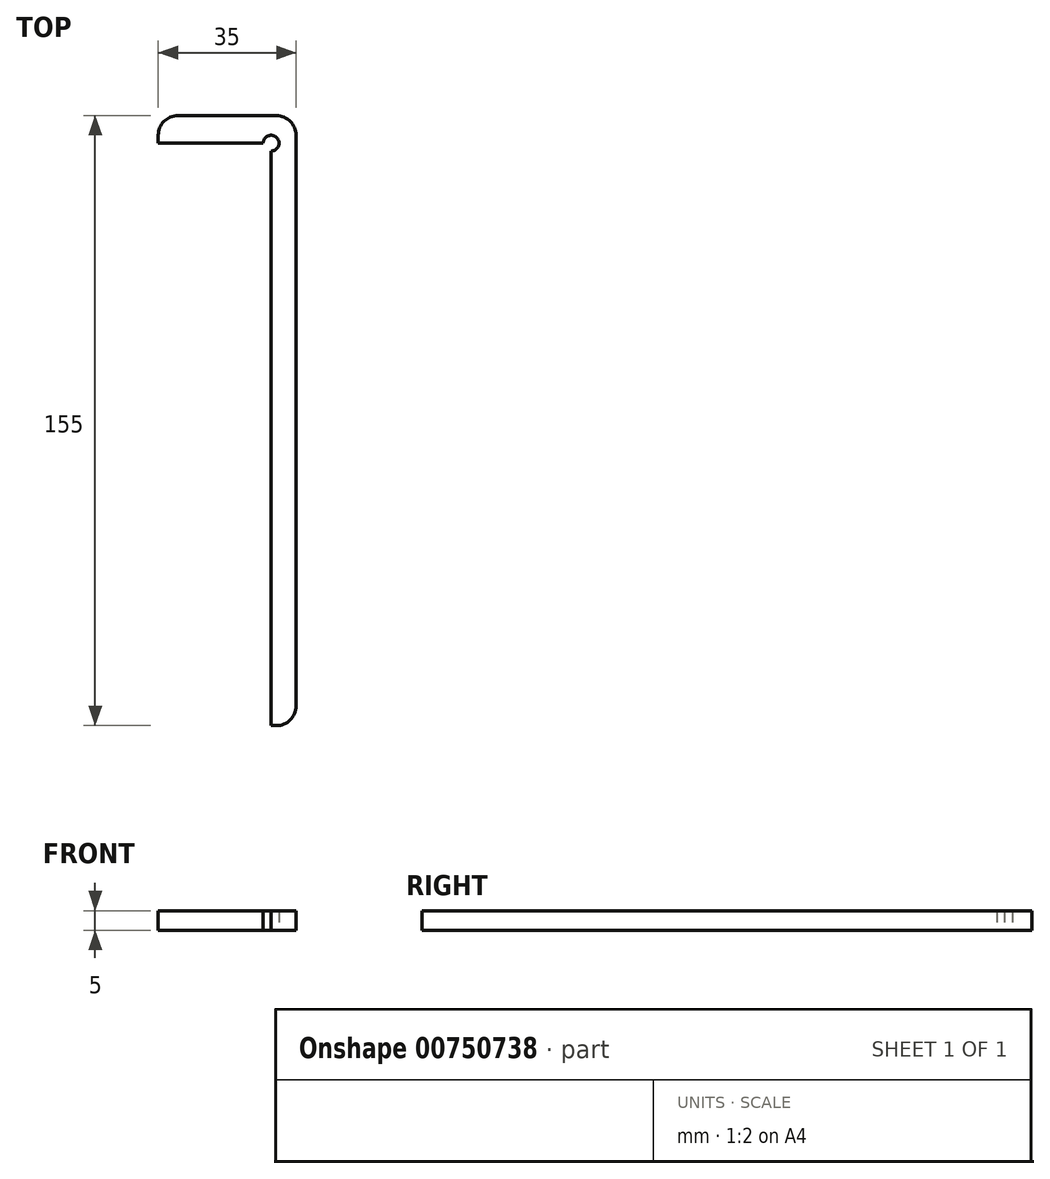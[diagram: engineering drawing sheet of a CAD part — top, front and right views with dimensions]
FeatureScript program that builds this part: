
annotation { "Feature Type Name" : "Feature", "Feature Type Description" : "" }
export const myFeature = defineFeature(function(context is Context, id is Id, definition is map)
    precondition{}
    {
        {
            var Q0;
            Q0=qCreatedBy(makeId("Top.planeOp"),FACE);
            var sketch = newSketch(context, id + "F0", { "sketchPlane" : qUnion([Q0])});
            skLineSegment(sketch, "E0.bottom", {"start": v(17.5, -77.5) * mm, "end": v(-17.5, -77.5) * mm});
            skLineSegment(sketch, "E0.top", {"start": v(17.5, 77.5) * mm, "end": v(-17.5, 77.5) * mm});
            skLineSegment(sketch, "E0.left", {"start": v(17.5, -77.5) * mm, "end": v(17.5, 77.5) * mm});
            skLineSegment(sketch, "E0.right", {"start": v(-17.5, -77.5) * mm, "end": v(-17.5, 70.5) * mm, "construction": true});
            skPoint(sketch, "E0.middle", {"position": v(0, 0) * mm});
            skLineSegment(sketch, "E1.bottom", {"start": v(-17.5, 70.5) * mm, "end": v(9.17, 70.5) * mm});
            skLineSegment(sketch, "E1.top", {"start": v(-17.5, -77.5) * mm, "end": v(11.17, -77.5) * mm, "construction": true});
            skLineSegment(sketch, "E1.left", {"start": v(-17.5, 70.5) * mm, "end": v(-17.5, 70.5) * mm});
            skLineSegment(sketch, "E1.right", {"start": v(11.17, 70.5) * mm, "end": v(11.17, -77.5) * mm});
            skLineSegment(sketch, "E2", {"start": v(-17.5, 70.5) * mm, "end": v(-17.5, -77.5) * mm, "construction": true});
            skLineSegment(sketch, "E3", {"start": v(11.17, -77.5) * mm, "end": v(11.17, -77.5) * mm});
            skLineSegment(sketch, "E4", {"start": v(-17.5, 70.5) * mm, "end": v(-17.5, 77.5) * mm});
            skLineSegment(sketch, "E5", {"start": v(9.17, 70.5) * mm, "end": v(11.17, 70.5) * mm, "construction": true});
            skArc(sketch, "E6", {"start": v(9.17, 70.5) * mm, "mid": v(9.76, 69.09) * mm, "end": v(11.17, 68.5) * mm, "construction": true});
            skArc(sketch, "E7", {"start": v(11.17, 68.5) * mm, "mid": v(12.58, 71.91) * mm, "end": v(9.17, 70.5) * mm});
            skSolve(sketch);
        }
        {
            var Q0;
            Q0 = qSketchRegion(id + "F0", true);
            extrude(context, id + "F1", {"entities" : qUnion([Q0]), "depth" : 5 * mm, "offsetDistance" : 25 * mm});
        }
        {
            var Q0;
            Q0=makeQuery(id+"F1.opExtrude","SWEPT_EDGE",EDGE,{"disambiguationData":[OSD([sQuery(id+"F0.wireOp",EDGE,"E0.top"),sQuery(id+"F0.wireOp",EDGE,"E0.left")])]});
            var Q1;
            Q1=makeQuery(id+"F1.opExtrude","SWEPT_EDGE",EDGE,{"disambiguationData":[OSD([sQuery(id+"F0.wireOp",EDGE,"E0.top"),sQuery(id+"F0.wireOp",EDGE,"E4")])]});
            var Q2;
            Q2=makeQuery(id+"F1.opExtrude","SWEPT_EDGE",EDGE,{"disambiguationData":[OSD([sQuery(id+"F0.wireOp",EDGE,"E0.bottom"),sQuery(id+"F0.wireOp",EDGE,"E0.left")])]});
            fillet(context, id + "F2", {"entities" : qUnion([Q0, Q1, Q2]), "radius" : 5 * mm, "tangentPropagation" : true, "allowEdgeOverflow" : false});
        }
    });
